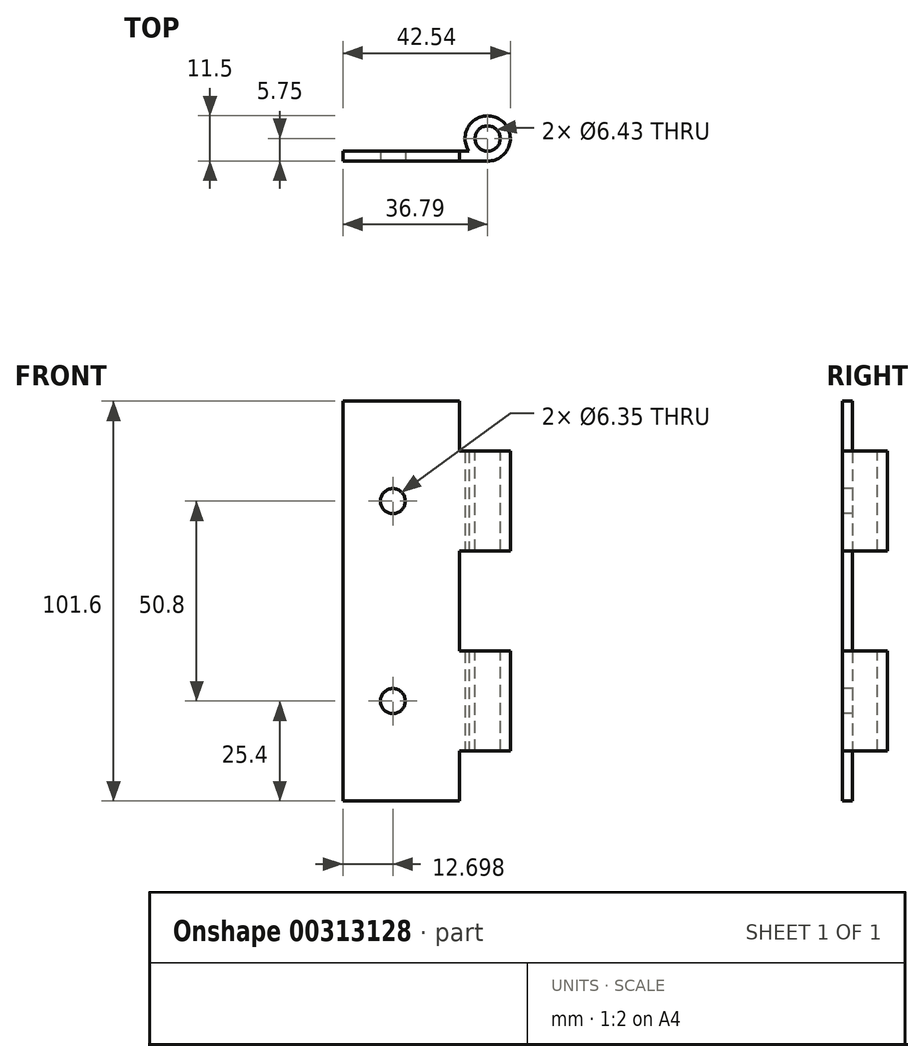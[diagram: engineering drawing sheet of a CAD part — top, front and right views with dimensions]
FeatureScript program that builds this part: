
annotation { "Feature Type Name" : "Feature", "Feature Type Description" : "" }
export const myFeature = defineFeature(function(context is Context, id is Id, definition is map)
    precondition{}
    {
        {
            var Q0;
            Q0=qCreatedBy(makeId("Top.planeOp"),FACE);
            var sketch = newSketch(context, id + "F0", { "sketchPlane" : qUnion([Q0])});
            skLineSegment(sketch, "E0", {"start": v(0, -5.75) * mm, "end": v(-36.8, -5.75) * mm});
            skLineSegment(sketch, "E1", {"start": v(-36.8, -5.75) * mm, "end": v(-36.8, -3.21) * mm});
            skLineSegment(sketch, "E2", {"start": v(-36.8, -3.21) * mm, "end": v(-4.77, -3.21) * mm});
            skArc(sketch, "E3", {"start": v(0, -5.75) * mm, "mid": v(2.7, 5.08) * mm, "end": v(-4.77, -3.21) * mm});
            skSolve(sketch);
        }
        {
            var Q0;
            Q0 = qSketchRegion(id + "F0", true);
            extrude(context, id + "F1", {"entities" : qUnion([Q0]), "endBound" : BoundingType.SYMMETRIC, "depth" : 101.6 * mm});
        }
        {
            var Q0;
            Q0=makeQuery(id+"F1.opExtrude","SWEPT_FACE",FACE,{"disambiguationData":[OSD([sQuery(id+"F0.wireOp",EDGE,"E0")])]});
            var sketch = newSketch(context, id + "F2", { "sketchPlane" : qUnion([Q0])});
            skLineSegment(sketch, "E4.bottom", {"start": v(18.2, 12.7) * mm, "end": v(-7.2, 12.7) * mm});
            skLineSegment(sketch, "E4.top", {"start": v(18.2, -12.7) * mm, "end": v(-7.2, -12.7) * mm});
            skLineSegment(sketch, "E4.left", {"start": v(18.2, 12.7) * mm, "end": v(18.2, -12.7) * mm});
            skLineSegment(sketch, "E4.right", {"start": v(-7.2, 12.7) * mm, "end": v(-7.2, -12.7) * mm});
            skPoint(sketch, "E4.middle", {"position": v(5.5, 0) * mm});
            skPoint(sketch, "E4.middle.positionSnap0", {"position": v(-36.8, 0) * mm});
            skPoint(sketch, "E4.centerSnap0", {"position": v(-36.8, 0) * mm});
            skLineSegment(sketch, "E5.bottom", {"start": v(-7.2, 38.1) * mm, "end": v(18.2, 38.1) * mm});
            skLineSegment(sketch, "E5.top", {"start": v(-7.2, 50.8) * mm, "end": v(18.2, 50.8) * mm});
            skLineSegment(sketch, "E5.left", {"start": v(-7.2, 38.1) * mm, "end": v(-7.2, 50.8) * mm});
            skLineSegment(sketch, "E5.right", {"start": v(18.2, 38.1) * mm, "end": v(18.2, 50.8) * mm});
            skLineSegment(sketch, "E6.bottom", {"start": v(-7.2, -38.1) * mm, "end": v(18.2, -38.1) * mm});
            skLineSegment(sketch, "E6.top", {"start": v(-7.2, -50.8) * mm, "end": v(18.2, -50.8) * mm});
            skLineSegment(sketch, "E6.left", {"start": v(-7.2, -38.1) * mm, "end": v(-7.2, -50.8) * mm});
            skLineSegment(sketch, "E6.right", {"start": v(18.2, -38.1) * mm, "end": v(18.2, -50.8) * mm});
            skCircle(sketch, "E7", {"center": v(-24.1, 25.4) * mm, "radius": 3.18 * mm});
            skCircle(sketch, "E8", {"center": v(-24.1, -25.4) * mm, "radius": 3.18 * mm});
            skSolve(sketch);
        }
        {
            var Q0;
            Q0 = qSketchRegion(id + "F2", true);
            extrude(context, id + "F3", {"entities" : qUnion([Q0]), "operationType" : NewBodyOperationType.REMOVE, "endBound" : BoundingType.THROUGH_ALL, "oppositeDirection" : true, "depth" : 25.4 * mm});
        }
        {
            var Q0;
            Q0=makeQuery(id+"F3.boolean.opBoolean","COPY",FACE,{"derivedFrom":makeQuery(id+"F3.opExtrude","SWEPT_FACE",FACE,{"disambiguationData":[OSD([sQuery(id+"F2.wireOp",EDGE,"E5.bottom")])]})});
            var sketch = newSketch(context, id + "F4", { "sketchPlane" : qUnion([Q0])});
            skCircle(sketch, "E9", {"center": v(0, 0) * mm, "radius": 3.21 * mm});
            skSolve(sketch);
        }
        {
            var Q0;
            Q0 = qSketchRegion(id + "F4", true);
            extrude(context, id + "F5", {"entities" : qUnion([Q0]), "operationType" : NewBodyOperationType.REMOVE, "endBound" : BoundingType.THROUGH_ALL, "oppositeDirection" : true, "depth" : 25.4 * mm});
        }
    });
